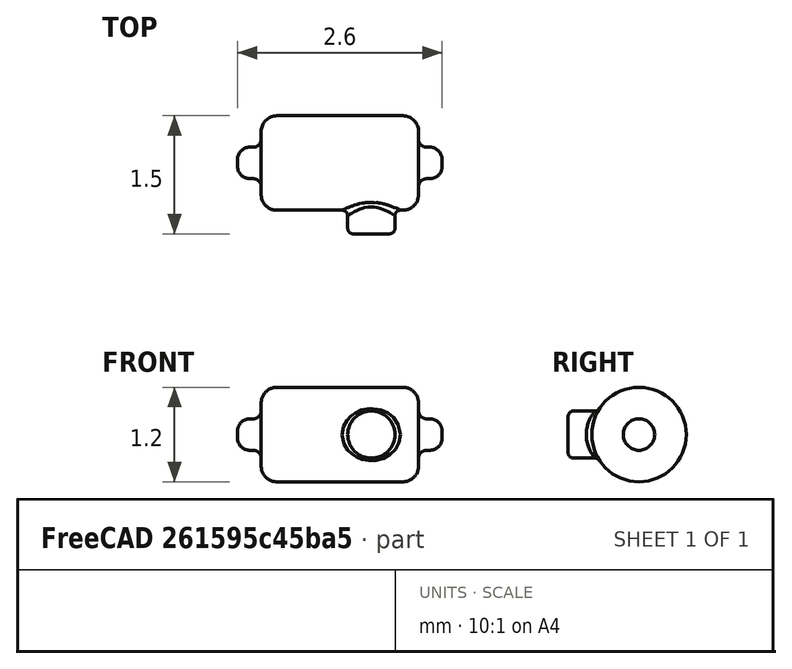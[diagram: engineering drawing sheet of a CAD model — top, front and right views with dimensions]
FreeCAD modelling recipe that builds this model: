
FCSTD DOCUMENT  (FreeCAD 0.16R6712 (Git))
Label: minusbulb
License: All rights reserved
LicenseURL: http://en.wikipedia.org/wiki/All_rights_reserved
objects: Sketcher::SketchObject×2, PartDesign::Revolution×1, PartDesign::Pad×1, Part::Fuse×1, PartDesign::Fillet×1, Mesh::Feature×1
note: 8 computed .brp shape members not serialized (recipe doc carries the construction recipe); baked Part::Feature solids carry a one-line shape summary decoded from their .brp

FEATURE [Sketcher::SketchObject] Sketch
  sketch-geometry (14):
    g0: LineSegment StartX=-1.14212 StartY=0.2 StartZ=0 EndX=-1.1 EndY=0.2 EndZ=0
    g1: LineSegment StartX=-1 StartY=0.4 StartZ=0 EndX=-1 EndY=0.3 EndZ=0
    g2: LineSegment StartX=-0.8 StartY=0.6 StartZ=0 EndX=0.8 EndY=0.6 EndZ=0
    g3: LineSegment StartX=1 StartY=0.4 StartZ=0 EndX=1 EndY=0.3 EndZ=0
    g4: LineSegment StartX=1.1 StartY=0.2 StartZ=0 EndX=1.14212 EndY=0.2 EndZ=0
    g5: LineSegment StartX=1.3 StartY=0.0421164 StartZ=0 EndX=1.3 EndY=0 EndZ=0
    g6: LineSegment StartX=1.3 StartY=0 StartZ=0 EndX=-1.3 EndY=0 EndZ=0
    g7: LineSegment StartX=-1.3 StartY=0 StartZ=0 EndX=-1.3 EndY=0.0421164 EndZ=0
    g8: ArcOfCircle CenterX=-1.1 CenterY=0.3 CenterZ=0 NormalX=0 NormalY=0 NormalZ=1 Radius=0.1 StartAngle=4.71239 EndAngle=6.28319
    g9: ArcOfCircle CenterX=-0.8 CenterY=0.4 CenterZ=0 NormalX=0 NormalY=0 NormalZ=1 Radius=0.2 StartAngle=1.5708 EndAngle=3.14159
    g10: ArcOfCircle CenterX=0.8 CenterY=0.4 CenterZ=0 NormalX=0 NormalY=0 NormalZ=1 Radius=0.2 StartAngle=0 EndAngle=1.5708
    g11: ArcOfCircle CenterX=1.1 CenterY=0.3 CenterZ=0 NormalX=0 NormalY=0 NormalZ=1 Radius=0.1 StartAngle=3.14159 EndAngle=4.71239
    g12: ArcOfCircle CenterX=1.14212 CenterY=0.0421164 CenterZ=0 NormalX=0 NormalY=0 NormalZ=1 Radius=0.157884 StartAngle=0 EndAngle=1.5708
    g13: ArcOfCircle CenterX=-1.14212 CenterY=0.0421164 CenterZ=0 NormalX=0 NormalY=0 NormalZ=1 Radius=0.157884 StartAngle=1.5708 EndAngle=3.14159
  constraints (34):
    c: Horizontal(g0)
    c: Horizontal(g4)
    c: Vertical(g5)
    c: PointOnObject(g6,g-1)
    c: Horizontal(g6)
    c: Vertical(g1)
    c: Vertical(g3)
    c: Vertical(g7)
    c: Tangent(g0,g8) = -1.5708
    c: Tangent(g1,g8) = 1.5708
    c: Tangent(g1,g9) = -1.5708
    c: Tangent(g2,g9) = 1.5708
    c: Tangent(g2,g10) = 1.5708
    c: Tangent(g3,g10) = 1.5708
    c: Tangent(g3,g11) = -1.5708
    c: Tangent(g4,g11) = -1.5708
    c: Tangent(g4,g12) = 1.5708
    c: Tangent(g5,g12) = 1.5708
    c: Coincident(g7,g6)
    c: Coincident(g5,g6)
    c: Symmetric(g5,g6,g-2)
    c: Radius(g10) = 0.2
    c: DistanceX(g-2,g5) = 1.3
    c: Distance(g-1,g4) = 0.2
    c: Distance(g-1,g0) = 0.2
    c: Distance(g-1,g2) = 0.6
    c: Symmetric(g9,g10,g-2)
    c: Equal(g10,g9)
    c: Equal(g11,g8)
    c: Radius(g8) = 0.1
    c: Distance(g-1,g3) = 1
    c: Tangent(g0,g13) = 1.5708
    c: Tangent(g7,g13) = 1.5708
    c: Equal(g12,g13)
FEATURE [PartDesign::Revolution] Revolution
  Angle = 360
  Axis = (1,0,0)
  Base = (0,0,0)
  ReferenceAxis = -> Sketch [H_Axis]
  Sketch = -> Sketch
FEATURE [Sketcher::SketchObject] Sketch001
  Placement = pos=(0,-0.5,0) rot=(1,0,0;1.5708rad)
  sketch-geometry (1):
    g0: Circle CenterX=0.4 CenterY=0 CenterZ=0 NormalX=0 NormalY=0 NormalZ=1 Radius=0.3
  constraints (3):
    c: PointOnObject(g0,g-1)
    c: Radius(g0) = 0.3
    c: DistanceX(g-2,g0) = 0.4
FEATURE [PartDesign::Pad] Pad
  Length = 0.4
  Length2 = 100
  Placement = pos=(0,-0.5,0) rot=(1,0,0;1.5708rad)
  Sketch = -> Sketch001
  Type = 0
FEATURE [Part::Fuse] Fusion
  Base = -> Pad
  Tool = -> Revolution
FEATURE [PartDesign::Fillet] Fillet
  Base = -> Fusion [Edge2,Edge1,Edge4,Edge3]
  Radius = 0.07
FEATURE [Mesh::Feature] Mesh  label="Fillet (Meshed)"
